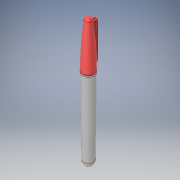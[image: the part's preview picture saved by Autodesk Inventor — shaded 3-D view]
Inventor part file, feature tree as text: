
AUTODESK INVENTOR PART (.ipt)
format: ipt  version: 2019 (Build 230136000, 136)  size: 224,768 bytes
history: native  units: in
note: dims shown in document units (in); Inventor stores cm internally (conversion verified against a paired STEP export)
features: sketch x2, extrude x2, revolve x1, chamfer x1, fillet x1
ambient origin geometry x8: Origin, YZ Plane, XZ Plane, XY Plane, X Axis, Y Axis, Z Axis, Center Point
bodies: Solid1 (feature_tree)
feature tree (7):
  revolve  "Revolution1"  [1 undecoded]
  sketch  "Sketch2"  dims[d3=2.0in d4=0.14in d5=0.025in d6=45.0deg d7=45.0deg d8=0.025in d9=0.025in d10=0.04in d11=0.2115in d12=90.0deg d14=0.0125in d15=0.12in d16=0.075in d17=0.12in d18=0.04in d19=0.15in d20=1.6in d21=0.375in d22=0.14in d23=0.0in d24=0.06in d25=0.0in d26=0.06in d27=0.125in d28=45.0deg d29=0.02in]
  extrude  "Extrusion1"  Depth=0.02in
  extrude  "Extrusion2"  Depth=0.02in
  chamfer  "Chamfer1"  Angle=45.0deg  [1 undecoded]
  fillet  "Fillet1"  [1 undecoded]
  sketch  "Sketch1"  dims[d0=0.48in d1=5.4in]
note: 3 required parameter values undecoded (feature->parameter linkage not recoverable at this tier; creation-order binding heuristic only, values carry confidence <= 0.55)